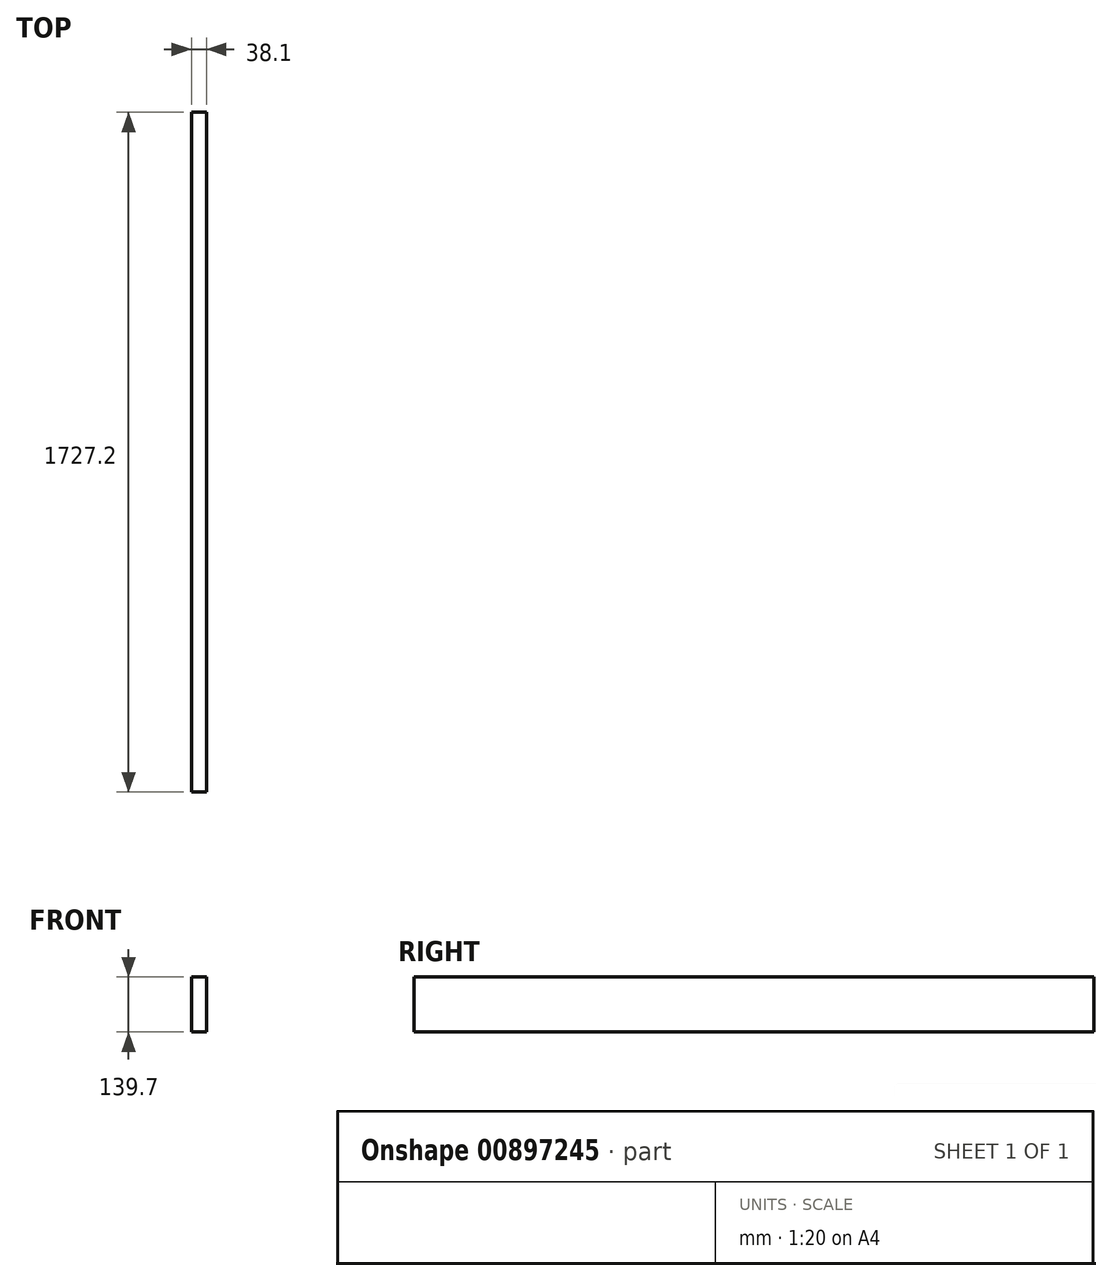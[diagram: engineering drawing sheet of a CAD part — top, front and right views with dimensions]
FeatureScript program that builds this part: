
annotation { "Feature Type Name" : "Feature", "Feature Type Description" : "" }
export const myFeature = defineFeature(function(context is Context, id is Id, definition is map)
    precondition{}
    {
        {
            var Q0;
            Q0=qCreatedBy(makeId("Front.planeOp"),FACE);
            var sketch = newSketch(context, id + "F0", { "sketchPlane" : qUnion([Q0])});
            skLineSegment(sketch, "E0.bottom", {"start": v(-19.05, 69.85) * mm, "end": v(19.05, 69.85) * mm});
            skLineSegment(sketch, "E0.top", {"start": v(-19.05, -69.85) * mm, "end": v(19.05, -69.85) * mm});
            skLineSegment(sketch, "E0.left", {"start": v(-19.05, 69.85) * mm, "end": v(-19.05, -69.85) * mm});
            skLineSegment(sketch, "E0.right", {"start": v(19.05, 69.85) * mm, "end": v(19.05, -69.85) * mm});
            skPoint(sketch, "E0.middle", {"position": v(0, 0) * mm});
            skSolve(sketch);
        }
        {
            var Q0;
            Q0=makeQuery(id+"F0.imprint","IMPRINT",FACE,{"disambiguationData":[TD([[makeQuery(id+"F0.imprint","IMPRINT",EDGE,{"derivedFrom":sQuery(id+"F0.wireOp",EDGE,"E0.bottom")}),-1.0]])]});
            extrude(context, id + "F1", {"entities" : qUnion([Q0]), "depth" : 1727.2 * mm, "offsetDistance" : 25.4 * mm});
        }
    });
